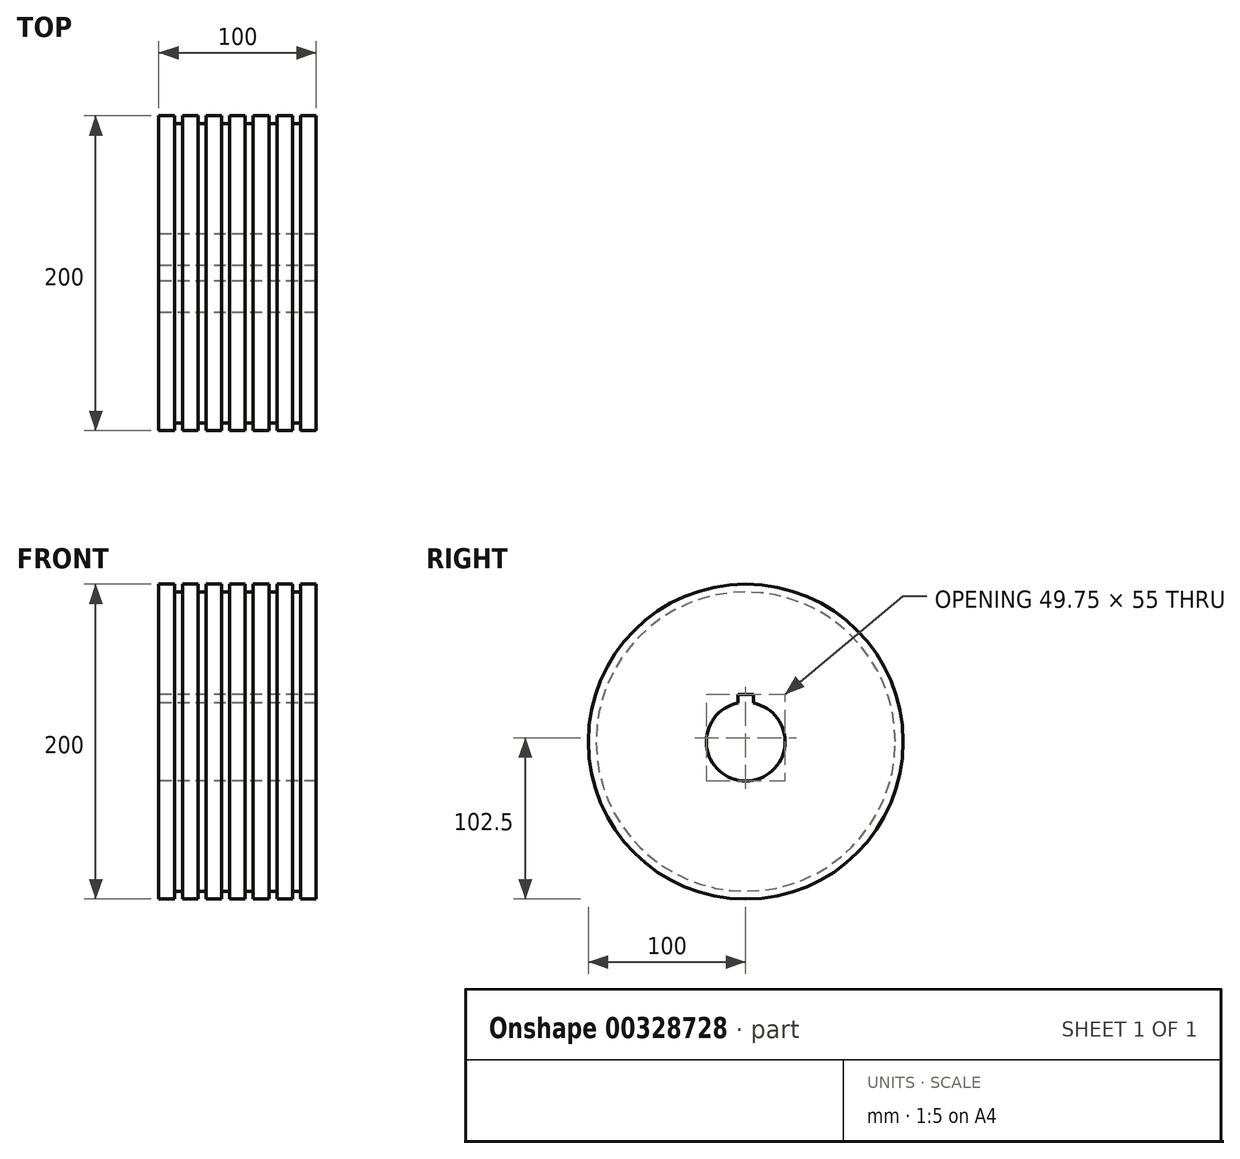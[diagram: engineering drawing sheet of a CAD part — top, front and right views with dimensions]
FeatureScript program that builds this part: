
annotation { "Feature Type Name" : "Feature", "Feature Type Description" : "" }
export const myFeature = defineFeature(function(context is Context, id is Id, definition is map)
    precondition{}
    {
        {
            var Q0;
            Q0=qCreatedBy(makeId("Front.planeOp"),FACE);
            var sketch = newSketch(context, id + "F0", { "sketchPlane" : qUnion([Q0])});
            skLineSegment(sketch, "E0.bottom", {"start": v(50, -50) * mm, "end": v(40, -50) * mm});
            skLineSegment(sketch, "E0.top", {"start": v(50, 50) * mm, "end": v(-50, 50) * mm});
            skLineSegment(sketch, "E0.left", {"start": v(50, -50) * mm, "end": v(50, 50) * mm});
            skLineSegment(sketch, "E0.right", {"start": v(-50, -50) * mm, "end": v(-50, 50) * mm});
            skPoint(sketch, "E0.middle", {"position": v(0, 0) * mm});
            skLineSegment(sketch, "E1", {"start": v(-40, -50) * mm, "end": v(-40, -45) * mm});
            skLineSegment(sketch, "E2", {"start": v(-40, -45) * mm, "end": v(-35, -45) * mm});
            skLineSegment(sketch, "E3", {"start": v(-35, -45) * mm, "end": v(-35, -50) * mm});
            skLineSegment(sketch, "E4", {"start": v(-25, -50) * mm, "end": v(-25, -45) * mm});
            skLineSegment(sketch, "E5", {"start": v(-35, -50) * mm, "end": v(-25, -50) * mm});
            skLineSegment(sketch, "E6", {"start": v(-25, -45) * mm, "end": v(-20, -45) * mm});
            skLineSegment(sketch, "E7", {"start": v(-20, -45) * mm, "end": v(-20, -50) * mm});
            skLineSegment(sketch, "E8", {"start": v(-10, -50) * mm, "end": v(-10, -45) * mm});
            skLineSegment(sketch, "E9", {"start": v(-10, -45) * mm, "end": v(-5, -45) * mm});
            skPoint(sketch, "E10.end.orphan", {"position": v(-8.13, -50) * mm});
            skLineSegment(sketch, "E11", {"start": v(-5, -45) * mm, "end": v(-5, -50) * mm});
            skLineSegment(sketch, "E12", {"start": v(5, -50) * mm, "end": v(5, -45) * mm});
            skLineSegment(sketch, "E13", {"start": v(5, -45) * mm, "end": v(10, -45) * mm});
            skLineSegment(sketch, "E14", {"start": v(10, -45) * mm, "end": v(10, -50) * mm});
            skLineSegment(sketch, "E15", {"start": v(20, -50) * mm, "end": v(20, -45) * mm});
            skLineSegment(sketch, "E16", {"start": v(20, -45) * mm, "end": v(25, -45) * mm});
            skLineSegment(sketch, "E17", {"start": v(25, -45) * mm, "end": v(25, -50) * mm});
            skLineSegment(sketch, "E18.trimOffspring", {"start": v(5, -50) * mm, "end": v(-5, -50) * mm});
            skLineSegment(sketch, "E19", {"start": v(35, -50) * mm, "end": v(35, -45) * mm});
            skPoint(sketch, "E19.endSnap0", {"position": v(22.5, -45) * mm});
            skLineSegment(sketch, "E20", {"start": v(35, -45) * mm, "end": v(40, -45) * mm});
            skLineSegment(sketch, "E21", {"start": v(40, -45) * mm, "end": v(40, -50) * mm});
            skLineSegment(sketch, "E22.trimOffspring", {"start": v(-10, -50) * mm, "end": v(-20, -50) * mm});
            skLineSegment(sketch, "E23.trimOffspring", {"start": v(-25, -50) * mm, "end": v(-35, -50) * mm});
            skLineSegment(sketch, "E24.trimOffspring", {"start": v(-40, -50) * mm, "end": v(-50, -50) * mm});
            skLineSegment(sketch, "E25.trimOffspring", {"start": v(20, -50) * mm, "end": v(10, -50) * mm});
            skLineSegment(sketch, "E26.trimOffspring", {"start": v(35, -50) * mm, "end": v(25, -50) * mm});
            skSolve(sketch);
        }
        {
            var Q0;
            Q0=makeQuery(id+"F0.imprint","IMPRINT",FACE,{"disambiguationData":[TD([[makeQuery(id+"F0.imprint","IMPRINT",EDGE,{"derivedFrom":sQuery(id+"F0.wireOp",EDGE,"E0.bottom")}),-1.0]])]});
            var Q1;
            Q1=sQuery(id+"F0.wireOp",EDGE,"E0.top");
            revolve(context, id + "F1", {"entities" : qUnion([Q0]), "axis" : qUnion([Q1]), "revolveType" : RevolveType.FULL});
        }
        {
            var Q0;
            Q0=makeQuery(id+"F1.opRevolve","SWEPT_FACE",FACE,{"disambiguationData":[OSD([sQuery(id+"F0.wireOp",EDGE,"E0.right")])]});
            var sketch = newSketch(context, id + "F2", { "sketchPlane" : qUnion([Q0])});
            skArc(sketch, "E27", {"start": v(-5, 74.5) * mm, "mid": v(0, 25) * mm, "end": v(5, 74.5) * mm});
            skLineSegment(sketch, "E28", {"start": v(0, 80) * mm, "end": v(-5, 80) * mm});
            skLineSegment(sketch, "E29", {"start": v(0, 80) * mm, "end": v(5, 80) * mm});
            skLineSegment(sketch, "E30", {"start": v(-5, 80) * mm, "end": v(-5, 74.5) * mm});
            skLineSegment(sketch, "E31", {"start": v(5, 80) * mm, "end": v(5, 74.5) * mm});
            skPoint(sketch, "E32.start.orphan", {"position": v(0, 75) * mm});
            skSolve(sketch);
        }
        {
            var Q0;
            Q0=makeQuery(id+"F2.imprint","IMPRINT",FACE,{"disambiguationData":[TD([[makeQuery(id+"F2.imprint","IMPRINT",EDGE,{"derivedFrom":sQuery(id+"F2.wireOp",EDGE,"E27")}),1.0]])]});
            extrude(context, id + "F3", {"entities" : qUnion([Q0]), "operationType" : NewBodyOperationType.REMOVE, "oppositeDirection" : true, "depth" : 100 * mm});
        }
    });
